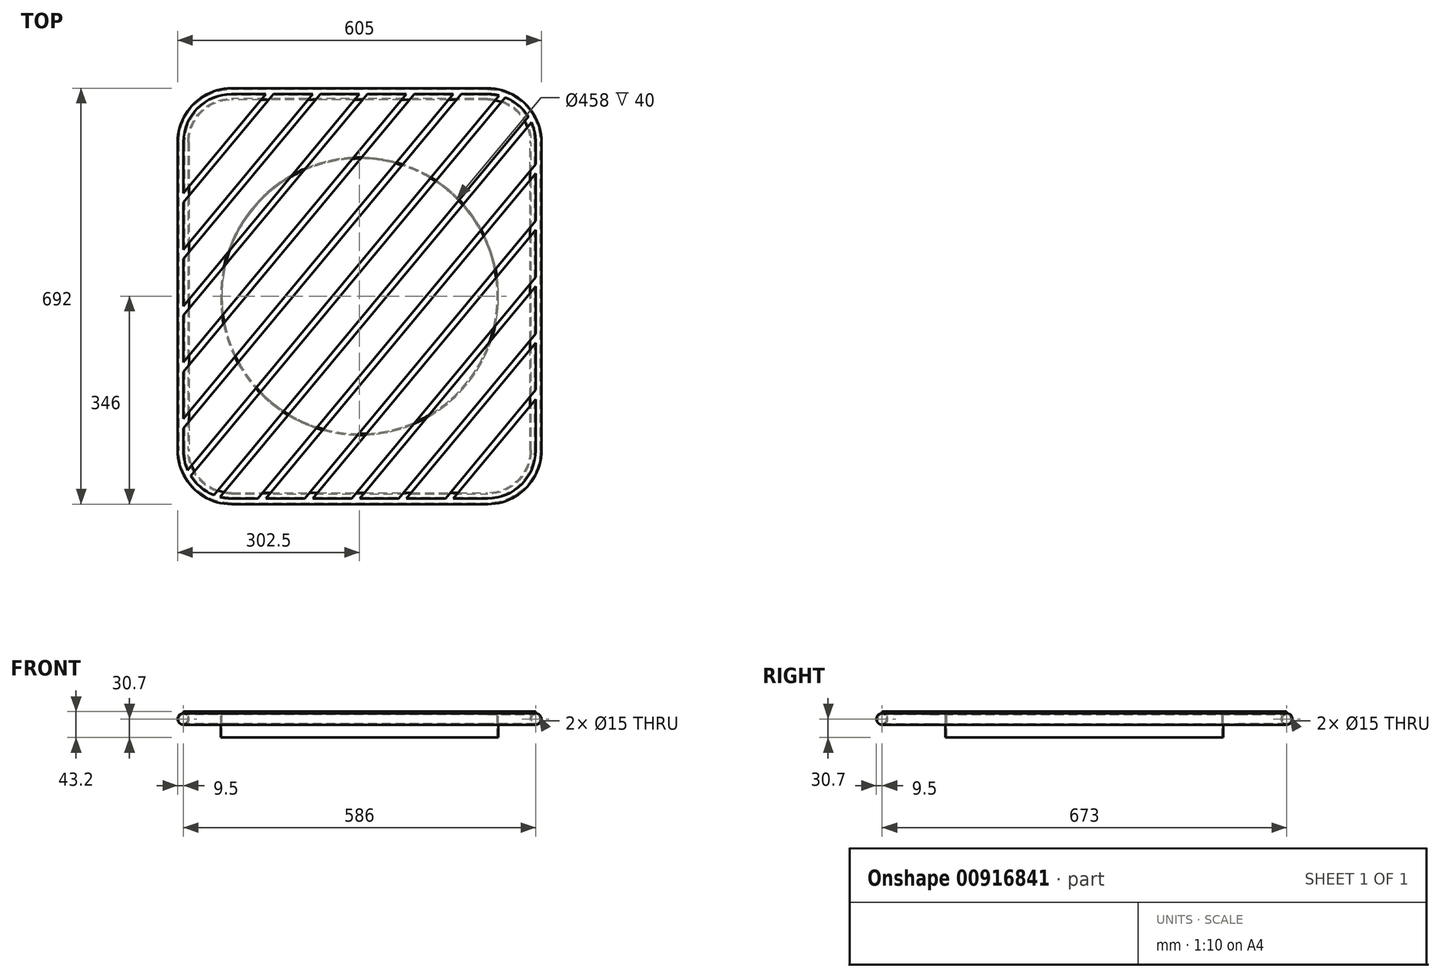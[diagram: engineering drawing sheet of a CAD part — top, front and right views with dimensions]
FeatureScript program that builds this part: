
annotation { "Feature Type Name" : "Feature", "Feature Type Description" : "" }
export const myFeature = defineFeature(function(context is Context, id is Id, definition is map)
    precondition{}
    {
        {
            var Q0;
            Q0=qCreatedBy(makeId("Top.planeOp"),FACE);
            var sketch = newSketch(context, id + "F0", { "sketchPlane" : qUnion([Q0])});
            skLineSegment(sketch, "E0.bottom", {"start": v(-213, 336.5) * mm, "end": v(213, 336.5) * mm});
            skLineSegment(sketch, "E0.top", {"start": v(-213, -336.5) * mm, "end": v(213, -336.5) * mm});
            skLineSegment(sketch, "E0.left", {"start": v(-293, 256.5) * mm, "end": v(-293, -256.5) * mm});
            skLineSegment(sketch, "E0.right", {"start": v(293, 256.5) * mm, "end": v(293, -256.5) * mm});
            skPoint(sketch, "E0.middle", {"position": v(0, 0) * mm});
            skArc(sketch, "E1", {"start": v(-213, 336.5) * mm, "mid": v(-269.57, 313.07) * mm, "end": v(-293, 256.5) * mm});
            skArc(sketch, "E2", {"start": v(293, 256.5) * mm, "mid": v(269.57, 313.07) * mm, "end": v(213, 336.5) * mm});
            skPoint(sketch, "E3.orphan", {"position": v(-293, 336.5) * mm});
            skPoint(sketch, "E4.orphan", {"position": v(293, 336.5) * mm});
            skArc(sketch, "E5.MirrorCS", {"start": v(293, -256.5) * mm, "mid": v(269.57, -313.07) * mm, "end": v(213, -336.5) * mm});
            skArc(sketch, "E6.MirrorCS", {"start": v(-213, -336.5) * mm, "mid": v(-269.57, -313.07) * mm, "end": v(-293, -256.5) * mm});
            skPoint(sketch, "E7.orphan", {"position": v(-293, -336.5) * mm});
            skPoint(sketch, "E8.orphan", {"position": v(293, -336.5) * mm});
            skSolve(sketch);
        }
        {
            var Q0;
            Q0=qCreatedBy(makeId("Front.planeOp"),FACE);
            var sketch = newSketch(context, id + "F1", { "sketchPlane" : qUnion([Q0])});
            skCircle(sketch, "E9", {"center": v(-293, 0) * mm, "radius": 9.5 * mm});
            skCircle(sketch, "E10", {"center": v(-293, 0) * mm, "radius": 7.5 * mm});
            skSolve(sketch);
        }
        {
            var Q0;
            Q0=makeQuery(id+"F1.imprint","IMPRINT",FACE,{"disambiguationData":[TD([[makeQuery(id+"F1.imprint","IMPRINT",EDGE,{"derivedFrom":sQuery(id+"F1.wireOp",EDGE,"E9")}),1.0]])]});
            var Q1;
            Q1=sQuery(id+"F0.wireOp",EDGE,"E0.left");
            var Q2;
            Q2=sQuery(id+"F0.wireOp",EDGE,"E1");
            var Q3;
            Q3=sQuery(id+"F0.wireOp",EDGE,"E0.bottom");
            var Q4;
            Q4=sQuery(id+"F0.wireOp",EDGE,"E2");
            var Q5;
            Q5=sQuery(id+"F0.wireOp",EDGE,"E0.right");
            var Q6;
            Q6=sQuery(id+"F0.wireOp",EDGE,"E5.MirrorCS");
            var Q7;
            Q7=sQuery(id+"F0.wireOp",EDGE,"E0.top");
            var Q8;
            Q8=sQuery(id+"F0.wireOp",EDGE,"E6.MirrorCS");
            sweep(context, id + "F2", {"profiles" : qUnion([Q0]), "path" : qUnion([Q1, Q2, Q3, Q4, Q5, Q6, Q7, Q8])});
        }
        {
            var Q0;
            Q0=qCreatedBy(makeId("Top.planeOp"),FACE);
            cPlane(context, id + "F3", {"entities" : qUnion([Q0]), "cplaneType" : CPlaneType.OFFSET, "offset" : 9.5 * mm, "width" : 150 * mm, "height" : 150 * mm});
        }
        {
            var Q0;
            Q0=qCreatedBy(id+"F3.planeOp",FACE);
            var sketch = newSketch(context, id + "F4", { "sketchPlane" : qUnion([Q0])});
            skLineSegment(sketch, "E11.bottom", {"start": v(-213, 336.5) * mm, "end": v(213, 336.5) * mm});
            skLineSegment(sketch, "E11.top", {"start": v(-213, -336.5) * mm, "end": v(213, -336.5) * mm});
            skLineSegment(sketch, "E11.left", {"start": v(-293, 256.5) * mm, "end": v(-293, -256.5) * mm});
            skLineSegment(sketch, "E11.right", {"start": v(293, 256.5) * mm, "end": v(293, -256.5) * mm});
            skPoint(sketch, "E11.middle", {"position": v(0, 0) * mm});
            skArc(sketch, "E12", {"start": v(293, 256.5) * mm, "mid": v(269.57, 313.07) * mm, "end": v(213, 336.5) * mm});
            skArc(sketch, "E13", {"start": v(-213, 336.5) * mm, "mid": v(-269.57, 313.07) * mm, "end": v(-293, 256.5) * mm});
            skPoint(sketch, "E14.orphan", {"position": v(293, 336.5) * mm});
            skPoint(sketch, "E15.orphan", {"position": v(-293, 336.5) * mm});
            skArc(sketch, "E16.MirrorCS", {"start": v(-213, -336.5) * mm, "mid": v(-269.57, -313.07) * mm, "end": v(-293, -256.5) * mm});
            skArc(sketch, "E17.MirrorCS", {"start": v(293, -256.5) * mm, "mid": v(269.57, -313.07) * mm, "end": v(213, -336.5) * mm});
            skPoint(sketch, "E18.orphan", {"position": v(-293, -336.5) * mm});
            skPoint(sketch, "E19.orphan", {"position": v(293, -336.5) * mm});
            skLineSegment(sketch, "E20", {"start": v(242.32, 330.94) * mm, "end": v(-280.78, -299) * mm});
            skLineSegment(sketch, "E21", {"start": v(-242.32, -330.94) * mm, "end": v(280.78, 299) * mm});
            skLineSegment(sketch, "E22", {"start": v(285.88, 289.48) * mm, "end": v(-232.03, -334.2) * mm});
            skLineSegment(sketch, "E23", {"start": v(-168.95, -336.5) * mm, "end": v(293, 219.79) * mm});
            skLineSegment(sketch, "E24", {"start": v(293, 204.13) * mm, "end": v(-155.95, -336.5) * mm});
            skLineSegment(sketch, "E25", {"start": v(-90.96, -336.5) * mm, "end": v(293, 125.87) * mm});
            skLineSegment(sketch, "E26", {"start": v(293, 110.22) * mm, "end": v(-77.96, -336.5) * mm});
            skLineSegment(sketch, "E27", {"start": v(-12.97, -336.5) * mm, "end": v(293, 31.95) * mm});
            skLineSegment(sketch, "E28", {"start": v(293, 16.3) * mm, "end": v(0.03, -336.5) * mm});
            skLineSegment(sketch, "E29", {"start": v(293, -61.97) * mm, "end": v(65.02, -336.5) * mm});
            skLineSegment(sketch, "E30", {"start": v(293, -77.62) * mm, "end": v(78.02, -336.5) * mm});
            skLineSegment(sketch, "E31", {"start": v(293, -155.88) * mm, "end": v(143.01, -336.5) * mm});
            skLineSegment(sketch, "E32", {"start": v(293, -171.54) * mm, "end": v(156.01, -336.5) * mm});
            skLineSegment(sketch, "E33", {"start": v(292.74, -250.1) * mm, "end": v(221.37, -336.06) * mm});
            skLineSegment(sketch, "E34", {"start": v(232.03, 334.2) * mm, "end": v(-285.88, -289.48) * mm});
            skLineSegment(sketch, "E35", {"start": v(168.95, 336.5) * mm, "end": v(-293, -219.79) * mm});
            skLineSegment(sketch, "E36", {"start": v(-293, -204.13) * mm, "end": v(155.95, 336.5) * mm});
            skLineSegment(sketch, "E37", {"start": v(90.96, 336.5) * mm, "end": v(-293, -125.87) * mm});
            skLineSegment(sketch, "E38", {"start": v(-293, -110.22) * mm, "end": v(77.96, 336.5) * mm});
            skLineSegment(sketch, "E39", {"start": v(12.97, 336.5) * mm, "end": v(-293, -31.95) * mm});
            skLineSegment(sketch, "E40", {"start": v(-293, -16.3) * mm, "end": v(-0.03, 336.5) * mm});
            skLineSegment(sketch, "E41", {"start": v(-65.02, 336.5) * mm, "end": v(-293, 61.97) * mm});
            skLineSegment(sketch, "E42", {"start": v(-293, 77.62) * mm, "end": v(-78.02, 336.5) * mm});
            skLineSegment(sketch, "E43", {"start": v(-143.01, 336.5) * mm, "end": v(-293, 155.88) * mm});
            skLineSegment(sketch, "E44", {"start": v(-221.37, 336.06) * mm, "end": v(-292.74, 250.1) * mm});
            skLineSegment(sketch, "E45", {"start": v(-156.01, 336.5) * mm, "end": v(-293, 171.54) * mm});
            skLineSegment(sketch, "E46", {"start": v(-213, -256.5) * mm, "end": v(213, 256.5) * mm});
            skSolve(sketch);
        }
        {
            var Q0;
            {var subQ3=sQuery(id+"F4.wireOp",EDGE,"E44");Q0=makeQuery(id+"F4.imprint","IMPRINT",FACE,{"disambiguationData":[TD([[makeQuery(id+"F4.imprint","IMPRINT",EDGE,{"derivedFrom":subQ3}),1.0]])]});}
            var Q1;
            {var subQ0=sQuery(id+"F4.wireOp",EDGE,"E42");Q1=makeQuery(id+"F4.imprint","IMPRINT",FACE,{"disambiguationData":[TD([[makeQuery(id+"F4.imprint","IMPRINT",EDGE,{"derivedFrom":subQ0}),1.0]])]});}
            var Q2;
            {var subQ0=sQuery(id+"F4.wireOp",EDGE,"E40");Q2=makeQuery(id+"F4.imprint","IMPRINT",FACE,{"disambiguationData":[TD([[makeQuery(id+"F4.imprint","IMPRINT",EDGE,{"derivedFrom":subQ0}),1.0]])]});}
            var Q3;
            {var subQ0=sQuery(id+"F4.wireOp",EDGE,"E38");Q3=makeQuery(id+"F4.imprint","IMPRINT",FACE,{"disambiguationData":[TD([[makeQuery(id+"F4.imprint","IMPRINT",EDGE,{"derivedFrom":subQ0}),1.0]])]});}
            var Q4;
            {var subQ0=sQuery(id+"F4.wireOp",EDGE,"E36");Q4=makeQuery(id+"F4.imprint","IMPRINT",FACE,{"disambiguationData":[TD([[makeQuery(id+"F4.imprint","IMPRINT",EDGE,{"derivedFrom":subQ0}),1.0]])]});}
            var Q5;
            {var subQ3=sQuery(id+"F4.wireOp",EDGE,"E34");Q5=makeQuery(id+"F4.imprint","IMPRINT",FACE,{"disambiguationData":[TD([[makeQuery(id+"F4.imprint","IMPRINT",EDGE,{"derivedFrom":subQ3}),-1.0]])]});}
            var Q6;
            Q6=makeQuery(id+"F4.imprint","IMPRINT",FACE,{"disambiguationData":[TD([[makeQuery(id+"F4.imprint","IMPRINT",EDGE,{"derivedFrom":sQuery(id+"F4.wireOp",EDGE,"E20")}),1.0]])]});
            var Q7;
            {var subQ3=sQuery(id+"F4.wireOp",EDGE,"E22");Q7=makeQuery(id+"F4.imprint","IMPRINT",FACE,{"disambiguationData":[TD([[makeQuery(id+"F4.imprint","IMPRINT",EDGE,{"derivedFrom":subQ3}),1.0]])]});}
            var Q8;
            {var subQ0=sQuery(id+"F4.wireOp",EDGE,"E24");Q8=makeQuery(id+"F4.imprint","IMPRINT",FACE,{"disambiguationData":[TD([[makeQuery(id+"F4.imprint","IMPRINT",EDGE,{"derivedFrom":subQ0}),1.0]])]});}
            var Q9;
            {var subQ0=sQuery(id+"F4.wireOp",EDGE,"E26");Q9=makeQuery(id+"F4.imprint","IMPRINT",FACE,{"disambiguationData":[TD([[makeQuery(id+"F4.imprint","IMPRINT",EDGE,{"derivedFrom":subQ0}),1.0]])]});}
            var Q10;
            {var subQ0=sQuery(id+"F4.wireOp",EDGE,"E28");Q10=makeQuery(id+"F4.imprint","IMPRINT",FACE,{"disambiguationData":[TD([[makeQuery(id+"F4.imprint","IMPRINT",EDGE,{"derivedFrom":subQ0}),1.0]])]});}
            var Q11;
            {var subQ0=sQuery(id+"F4.wireOp",EDGE,"E30");Q11=makeQuery(id+"F4.imprint","IMPRINT",FACE,{"disambiguationData":[TD([[makeQuery(id+"F4.imprint","IMPRINT",EDGE,{"derivedFrom":subQ0}),1.0]])]});}
            var Q12;
            {var subQ6=sQuery(id+"F4.wireOp",EDGE,"E45");Q12=makeQuery(id+"F4.imprint","IMPRINT",FACE,{"disambiguationData":[TD([[makeQuery(id+"F4.imprint","IMPRINT",EDGE,{"derivedFrom":subQ6}),-1.0]])]});}
            var Q13;
            {var subQ6=sQuery(id+"F4.wireOp",EDGE,"E32");Q13=makeQuery(id+"F4.imprint","IMPRINT",FACE,{"disambiguationData":[TD([[makeQuery(id+"F4.imprint","IMPRINT",EDGE,{"derivedFrom":subQ6}),1.0]])]});}
            extrude(context, id + "F5", {"entities" : qUnion([Q0, Q1, Q2, Q3, Q4, Q5, Q6, Q7, Q8, Q9, Q10, Q11, Q12, Q13]), "operationType" : NewBodyOperationType.ADD, "depth" : 3 * mm, "offsetDistance" : 25 * mm, "hasSecondDirection" : true, "secondDirectionOppositeDirection" : true, "secondDirectionDepth" : .2 * mm});
        }
        {
            var Q0;
            Q0=makeQuery(id+"F5.opExtrude","CAP_FACE",FACE,{"disambiguationData":[OSD([sQuery(id+"F4.wireOp",EDGE,"E20"),sQuery(id+"F4.wireOp",EDGE,"E21"),sQuery(id+"F4.wireOp",EDGE,"iFLLYgdB-dW7z-vr6p-lFbt-K6qCixQniB4U"),sQuery(id+"F4.wireOp",EDGE,"wFJiFnTN-CMnh-BemG-j1NL-eePKXfMXtu66")])],"isStart":true});
            var sketch = newSketch(context, id + "F6", { "sketchPlane" : qUnion([Q0])});
            skCircle(sketch, "E47", {"center": v(0, 0) * mm, "radius": 229 * mm});
            skCircle(sketch, "E48", {"center": v(0, 0) * mm, "radius": 231 * mm});
            skSolve(sketch);
        }
        {
            var Q0;
            Q0 = qSketchRegion(id + "F6", true);
            extrude(context, id + "F7", {"entities" : qUnion([Q0]), "operationType" : NewBodyOperationType.ADD, "depth" : 40 * mm, "offsetDistance" : 25 * mm});
        }
    });
